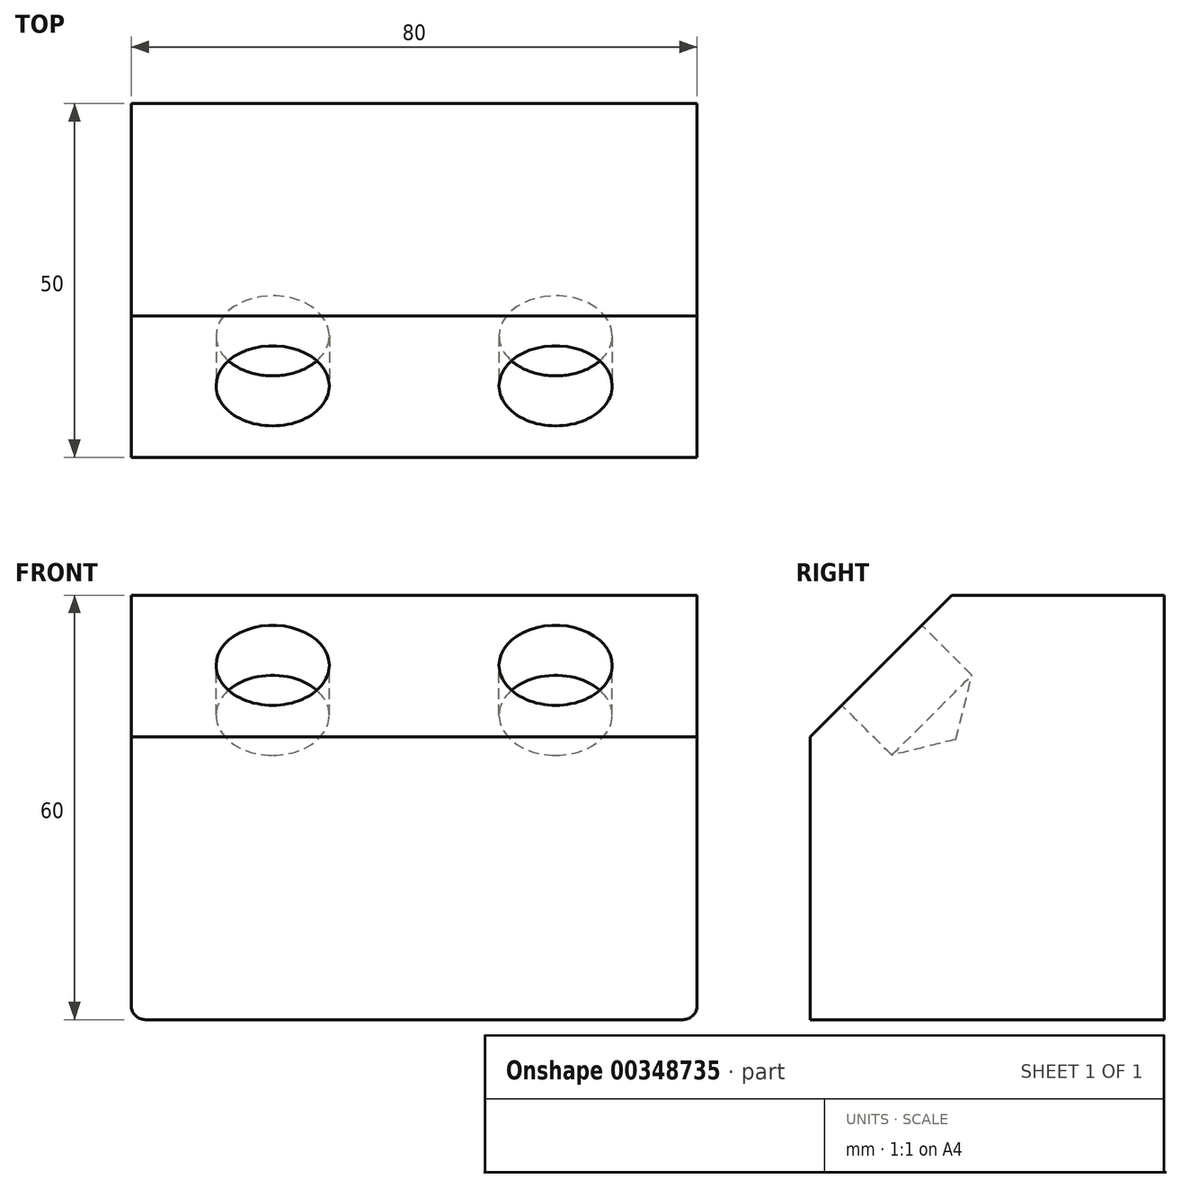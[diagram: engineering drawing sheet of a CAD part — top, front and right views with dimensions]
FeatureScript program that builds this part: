
annotation { "Feature Type Name" : "Feature", "Feature Type Description" : "" }
export const myFeature = defineFeature(function(context is Context, id is Id, definition is map)
    precondition{}
    {
        {
            var Q0;
            Q0=qCreatedBy(makeId("Top.planeOp"),FACE);
            var sketch = newSketch(context, id + "F0", { "sketchPlane" : qUnion([Q0])});
            skLineSegment(sketch, "E0.bottom", {"start": v(0, 0) * mm, "end": v(80, 0) * mm});
            skLineSegment(sketch, "E0.top", {"start": v(0, 50) * mm, "end": v(80, 50) * mm});
            skLineSegment(sketch, "E0.left", {"start": v(0, 0) * mm, "end": v(0, 50) * mm});
            skLineSegment(sketch, "E0.right", {"start": v(80, 0) * mm, "end": v(80, 50) * mm});
            skSolve(sketch);
        }
        {
            var Q0;
            Q0=makeQuery(id+"F0.imprint","IMPRINT",FACE,{"disambiguationData":[TD([[makeQuery(id+"F0.imprint","IMPRINT",EDGE,{"derivedFrom":sQuery(id+"F0.wireOp",EDGE,"E0.bottom")}),1.0]])]});
            extrude(context, id + "F1", {"entities" : qUnion([Q0]), "depth" : 60 * mm});
        }
        {
            var Q0;
            Q0=makeQuery(id+"F1.opExtrude","CAP_EDGE",EDGE,{"disambiguationData":[OSD([sQuery(id+"F0.wireOp",EDGE,"E0.bottom")])],"isStart":false});
            chamfer(context, id + "F2", {"entities" : qUnion([Q0]), "width" : 20 * mm, "tangentPropagation" : true});
        }
        {
            var Q0;
            Q0=makeQuery(id+"F2.opChamfer","BLEND_FACE",FACE,{"disambiguationData":[OSD([sQuery(id+"F0.wireOp",EDGE,"E0.bottom")])]});
            var sketch = newSketch(context, id + "F3", { "sketchPlane" : qUnion([Q0])});
            skPoint(sketch, "E1", {"position": v(20, 42.57) * mm});
            skPoint(sketch, "E2", {"position": v(60, 42.57) * mm});
            skSolve(sketch);
        }
        {
            var Q0;
            Q0=sQuery(id+"F3.wireOp",VERTEX,"E1");
            var Q1;
            Q1=sQuery(id+"F3.wireOp",VERTEX,"E2");
            var Q2;
            Q2=makeQuery(id+"F1.opExtrude","SWEPT_BODY",BODY,{"disambiguationData":[OSD([sQuery(id+"F0.wireOp",EDGE,"E0.bottom"),sQuery(id+"F0.wireOp",EDGE,"E0.top"),sQuery(id+"F0.wireOp",EDGE,"E0.left"),sQuery(id+"F0.wireOp",EDGE,"E0.right")])]});
            hole(context, id + "F4", {"style" : HoleStyle.SIMPLE, "endStyle" : HoleEndStyle.BLIND, "holeDiameter" : 16 * mm, "holeDepth" : 10 * mm, "isTappedThrough" : true, "tappedDepth" : 12 * mm, "tapClearance" : 3, "locations" : qUnion([Q0, Q1]), "scope" : qUnion([Q2])});
        }
        {
            var Q0;
            Q0=makeQuery(id+"F1.opExtrude","CAP_EDGE",EDGE,{"disambiguationData":[OSD([sQuery(id+"F0.wireOp",EDGE,"E0.right")])],"isStart":true});
            fillet(context, id + "F5", {"entities" : qUnion([Q0]), "radius" : 2 * mm, "tangentPropagation" : true, "allowEdgeOverflow" : false});
        }
        {
            var Q0;
            Q0=makeQuery(id+"F1.opExtrude","CAP_EDGE",EDGE,{"disambiguationData":[OSD([sQuery(id+"F0.wireOp",EDGE,"E0.left")])],"isStart":true});
            fillet(context, id + "F6", {"entities" : qUnion([Q0]), "radius" : 2 * mm, "tangentPropagation" : true, "allowEdgeOverflow" : false});
        }
    });
